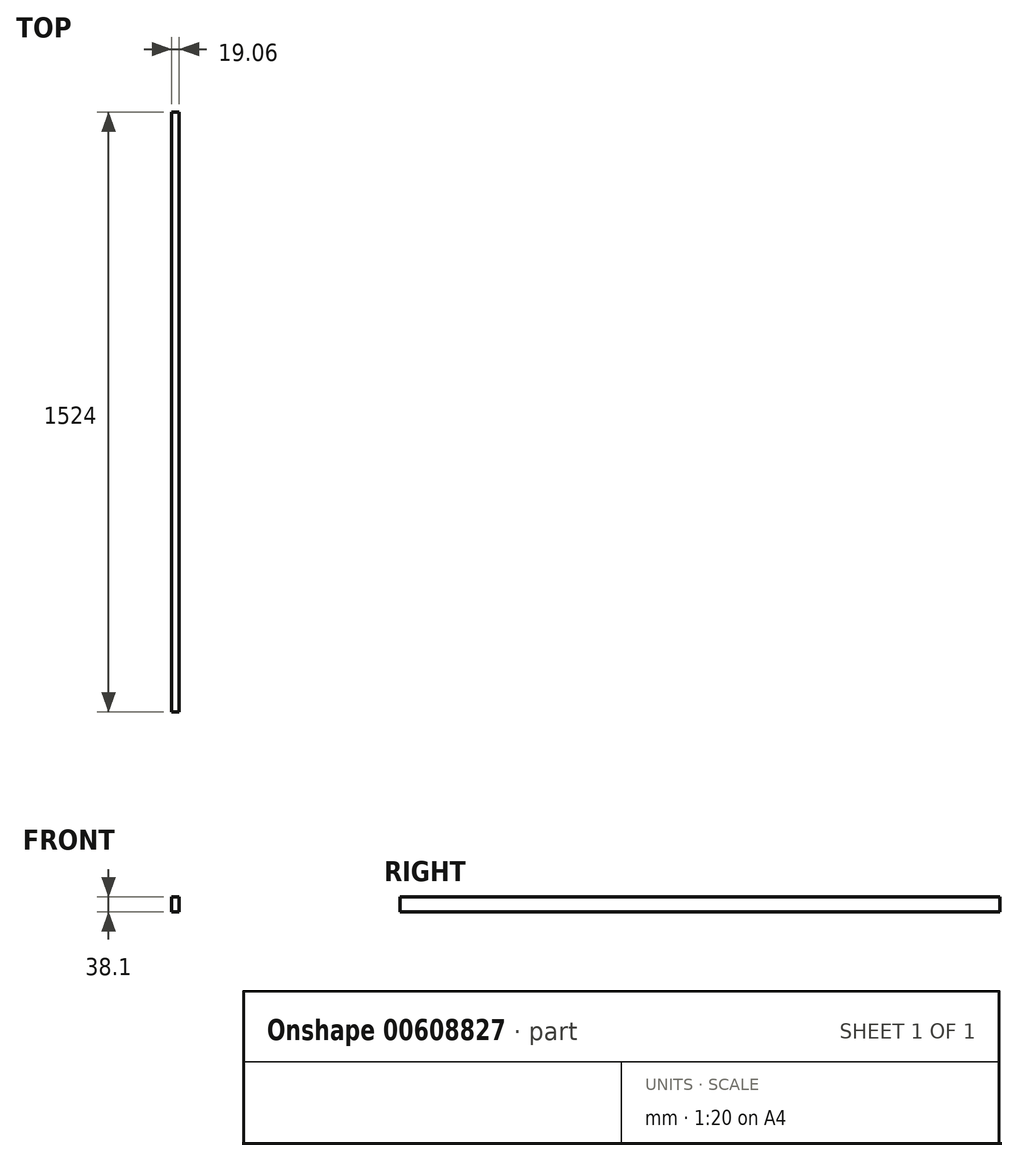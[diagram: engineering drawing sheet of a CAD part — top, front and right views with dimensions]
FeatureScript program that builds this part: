
annotation { "Feature Type Name" : "Feature", "Feature Type Description" : "" }
export const myFeature = defineFeature(function(context is Context, id is Id, definition is map)
    precondition{}
    {
        {
            var Q0;
            Q0=qCreatedBy(makeId("Front.planeOp"),FACE);
            var sketch = newSketch(context, id + "F0", { "sketchPlane" : qUnion([Q0])});
            skLineSegment(sketch, "E0.bottom", {"start": v(9.52, 19.05) * mm, "end": v(-9.53, 19.05) * mm});
            skLineSegment(sketch, "E0.top", {"start": v(9.53, -19.05) * mm, "end": v(-9.52, -19.05) * mm});
            skLineSegment(sketch, "E0.left", {"start": v(9.52, 19.05) * mm, "end": v(9.53, -19.05) * mm});
            skLineSegment(sketch, "E0.right", {"start": v(-9.53, 19.05) * mm, "end": v(-9.52, -19.05) * mm});
            skPoint(sketch, "E0.middle", {"position": v(0, 0) * mm});
            skSolve(sketch);
        }
        {
            var Q0;
            Q0 = qSketchRegion(id + "F0", true);
            extrude(context, id + "F1", {"entities" : qUnion([Q0]), "endBound" : BoundingType.SYMMETRIC, "depth" : 1524 * mm, "offsetDistance" : 25.4 * mm});
        }
    });
